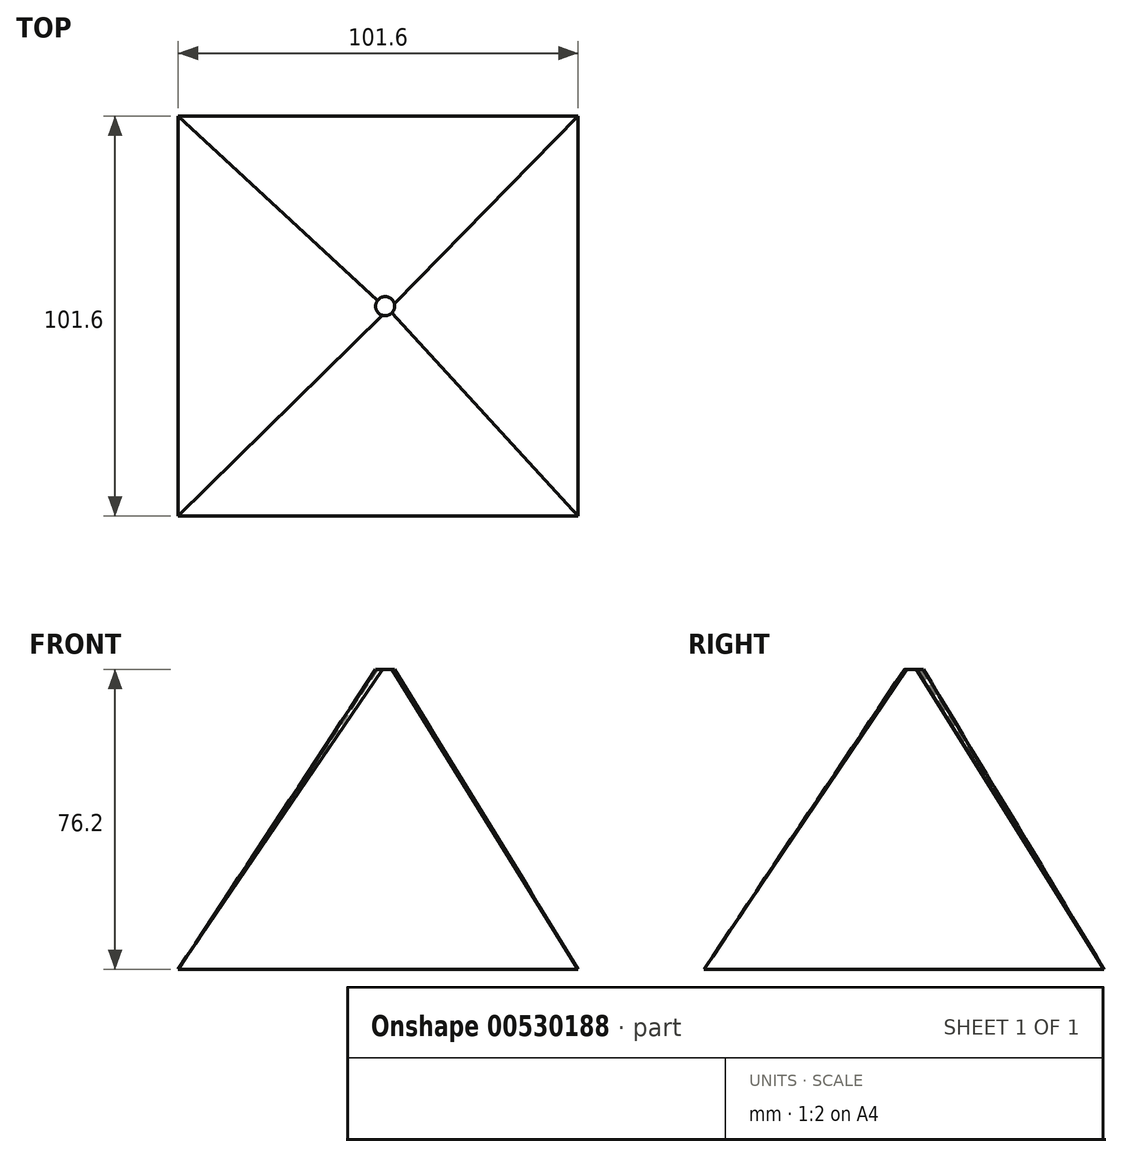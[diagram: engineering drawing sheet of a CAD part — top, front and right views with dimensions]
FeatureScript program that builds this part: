
annotation { "Feature Type Name" : "Feature", "Feature Type Description" : "" }
export const myFeature = defineFeature(function(context is Context, id is Id, definition is map)
    precondition{}
    {
        {
            var Q0;
            Q0=qCreatedBy(makeId("Top.planeOp"),FACE);
            var sketch = newSketch(context, id + "F0", { "sketchPlane" : qUnion([Q0])});
            skLineSegment(sketch, "E0.bottom", {"start": v(-34.9, 48.3) * mm, "end": v(66.7, 48.3) * mm});
            skLineSegment(sketch, "E0.top", {"start": v(-34.9, -53.3) * mm, "end": v(66.7, -53.3) * mm});
            skLineSegment(sketch, "E0.left", {"start": v(-34.9, 48.3) * mm, "end": v(-34.9, -53.3) * mm});
            skLineSegment(sketch, "E0.right", {"start": v(66.7, 48.3) * mm, "end": v(66.7, -53.3) * mm});
            skSolve(sketch);
        }
        {
            var Q0;
            Q0=qCreatedBy(makeId("Top.planeOp"),FACE);
            cPlane(context, id + "F1", {"entities" : qUnion([Q0]), "cplaneType" : CPlaneType.OFFSET, "offset" : 76.2 * mm, "width" : 152.4 * mm, "height" : 152.4 * mm});
        }
        {
            var Q0;
            Q0=qCreatedBy(id+"F1.planeOp",FACE);
            var sketch = newSketch(context, id + "F2", { "sketchPlane" : qUnion([Q0])});
            skArc(sketch, "E1", {"start": v(15.75, 1.47) * mm, "mid": v(15.37, -0.74) * mm, "end": v(16.96, -2.32) * mm});
            skArc(sketch, "E2", {"start": v(20, 0.66) * mm, "mid": v(18.13, 2.38) * mm, "end": v(15.75, 1.47) * mm});
            skArc(sketch, "E3", {"start": v(16.96, -2.32) * mm, "mid": v(19.37, -1.73) * mm, "end": v(20, 0.66) * mm});
            skSolve(sketch);
        }
        {
            var Q0;
            Q0=makeQuery(id+"F2.imprint","IMPRINT",FACE,{"disambiguationData":[TD([[makeQuery(id+"F2.imprint","IMPRINT",EDGE,{"derivedFrom":sQuery(id+"F2.wireOp",EDGE,"E1")}),1.0]])]});
            var Q1;
            Q1=makeQuery(id+"F0.imprint","IMPRINT",FACE,{"disambiguationData":[TD([[makeQuery(id+"F0.imprint","IMPRINT",EDGE,{"derivedFrom":sQuery(id+"F0.wireOp",EDGE,"E0.bottom")}),-1.0]])]});
            loft(context, id + "F3", {"sheetProfilesArray" : [{ "sheetProfileEntities" : qUnion([Q0]) }, { "sheetProfileEntities" : qUnion([Q1]) }]});
        }
    });
